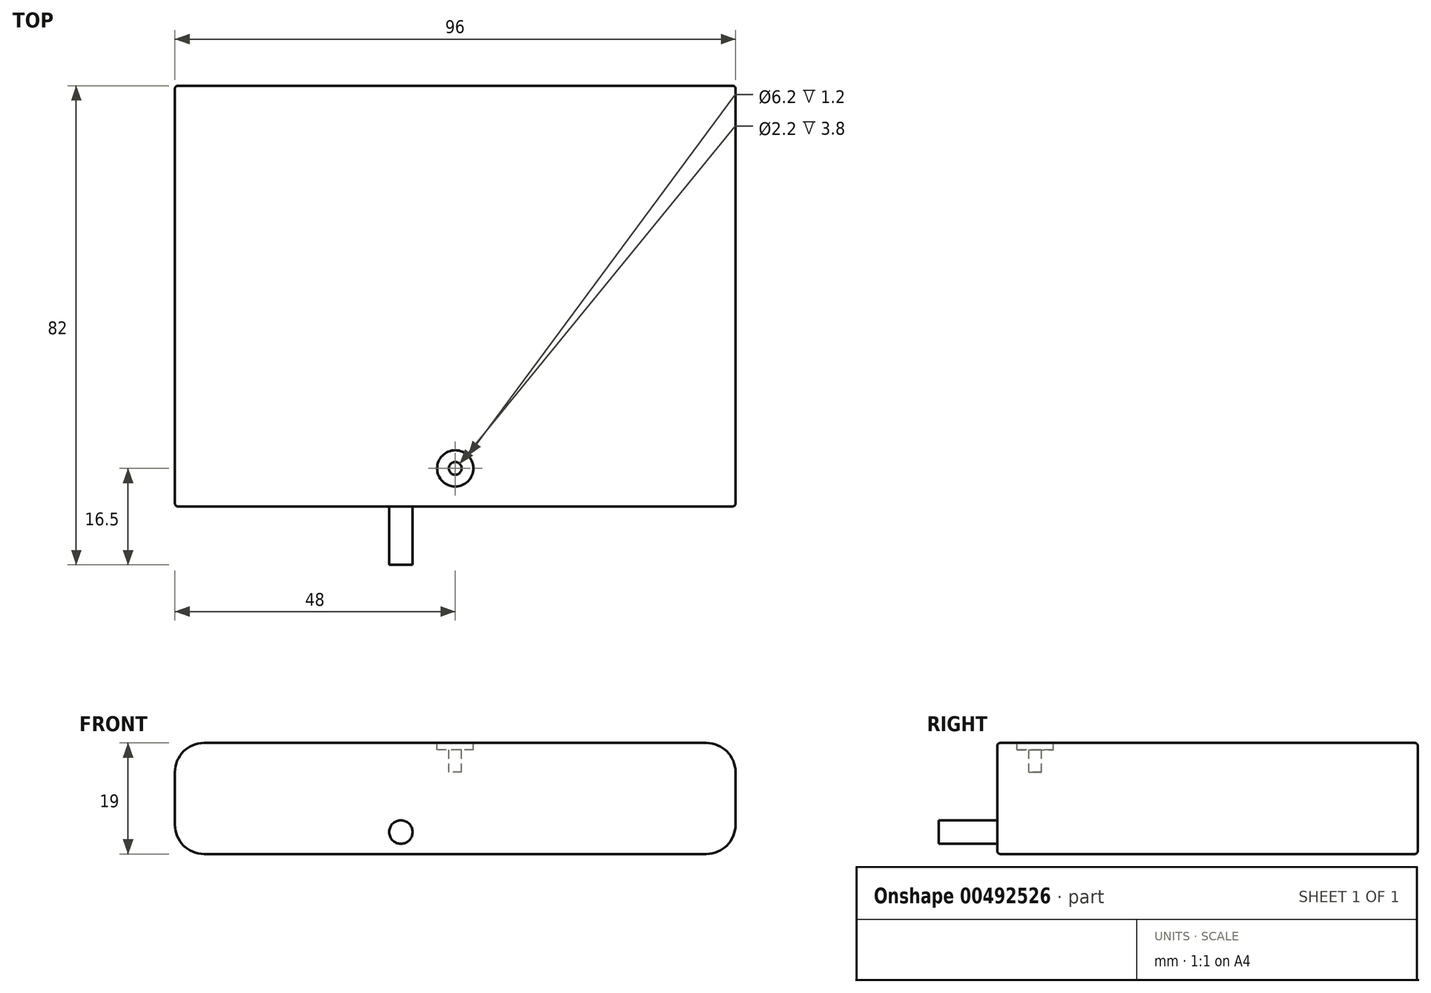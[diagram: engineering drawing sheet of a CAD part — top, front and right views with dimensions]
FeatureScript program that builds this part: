
annotation { "Feature Type Name" : "Feature", "Feature Type Description" : "" }
export const myFeature = defineFeature(function(context is Context, id is Id, definition is map)
    precondition{}
    {
        {
            var Q0;
            Q0=qCreatedBy(makeId("Top.planeOp"),FACE);
            var sketch = newSketch(context, id + "F0", { "sketchPlane" : qUnion([Q0])});
            skLineSegment(sketch, "E0.bottom", {"start": v(48, 36) * mm, "end": v(-48, 36) * mm});
            skLineSegment(sketch, "E0.top", {"start": v(48, -36) * mm, "end": v(-48, -36) * mm});
            skLineSegment(sketch, "E0.left", {"start": v(48, 36) * mm, "end": v(48, -36) * mm});
            skLineSegment(sketch, "E0.right", {"start": v(-48, 36) * mm, "end": v(-48, -36) * mm});
            skPoint(sketch, "E0.middle", {"position": v(0, 0) * mm});
            skSolve(sketch);
        }
        {
            var Q0;
            Q0=qSketchRegion(id+"F0",true);
            extrude(context, id + "F1", {"entities" : qUnion([Q0]), "depth" : 19 * mm});
        }
        {
            var Q0;
            Q0=makeQuery(id+"F1.opExtrude","CAP_EDGE",EDGE,{"disambiguationData":[OSD([sQuery(id+"F0.wireOp",EDGE,"E0.left")])],"isStart":false});
            var Q1;
            Q1=makeQuery(id+"F1.opExtrude","CAP_EDGE",EDGE,{"disambiguationData":[OSD([sQuery(id+"F0.wireOp",EDGE,"E0.left")])],"isStart":true});
            var Q2;
            Q2=makeQuery(id+"F1.opExtrude","CAP_EDGE",EDGE,{"disambiguationData":[OSD([sQuery(id+"F0.wireOp",EDGE,"E0.right")])],"isStart":false});
            var Q3;
            Q3=makeQuery(id+"F1.opExtrude","CAP_EDGE",EDGE,{"disambiguationData":[OSD([sQuery(id+"F0.wireOp",EDGE,"E0.right")])],"isStart":true});
            fillet(context, id + "F2", {"entities" : qUnion([Q0, Q1, Q2, Q3]), "radius" : 5 * mm, "tangentPropagation" : true, "allowEdgeOverflow" : false});
        }
        {
            var Q0;
            Q0=makeQuery(id+"F1.opExtrude","SWEPT_FACE",FACE,{"disambiguationData":[OSD([sQuery(id+"F0.wireOp",EDGE,"E0.top")])]});
            var Q1;
            Q1=makeQuery(id+"F1.opExtrude","SWEPT_FACE",FACE,{"disambiguationData":[OSD([sQuery(id+"F0.wireOp",EDGE,"E0.bottom")])]});
            fillet(context, id + "F3", {"entities" : qUnion([Q0, Q1]), "radius" : .5 * mm, "tangentPropagation" : true, "allowEdgeOverflow" : false});
        }
        {
            var Q0;
            Q0=makeQuery(id+"F1.opExtrude","SWEPT_FACE",FACE,{"disambiguationData":[OSD([sQuery(id+"F0.wireOp",EDGE,"E0.top")])]});
            var sketch = newSketch(context, id + "F4", { "sketchPlane" : qUnion([Q0])});
            skCircle(sketch, "E1", {"center": v(-9.3, 3.75) * mm, "radius": 2 * mm});
            skSolve(sketch);
        }
        {
            var Q0;
            Q0=qSketchRegion(id+"F4",true);
            extrude(context, id + "F5", {"entities" : qUnion([Q0]), "operationType" : NewBodyOperationType.ADD, "depth" : 10 * mm});
        }
        {
            var Q0;
            Q0=makeQuery(id+"F1.opExtrude","CAP_FACE",FACE,{"disambiguationData":[OSD([sQuery(id+"F0.wireOp",EDGE,"E0.bottom"),sQuery(id+"F0.wireOp",EDGE,"E0.top"),sQuery(id+"F0.wireOp",EDGE,"E0.left"),sQuery(id+"F0.wireOp",EDGE,"E0.right")])],"isStart":false});
            var sketch = newSketch(context, id + "F6", { "sketchPlane" : qUnion([Q0])});
            skCircle(sketch, "E2", {"center": v(0, -29.5) * mm, "radius": 3.1 * mm});
            skCircle(sketch, "E3", {"center": v(0, -29.5) * mm, "radius": 1.1 * mm});
            skSolve(sketch);
        }
        {
            var Q0;
            Q0=makeQuery(id+"F6.imprint","IMPRINT",FACE,{"disambiguationData":[TD([[makeQuery(id+"F6.imprint","IMPRINT",EDGE,{"derivedFrom":sQuery(id+"F6.wireOp",EDGE,"E3")}),1.0]])]});
            extrude(context, id + "F7", {"entities" : qUnion([Q0]), "operationType" : NewBodyOperationType.REMOVE, "oppositeDirection" : true, "depth" : 5 * mm});
        }
        {
            var Q0;
            Q0=makeQuery(id+"F6.imprint","IMPRINT",FACE,{"disambiguationData":[TD([[makeQuery(id+"F6.imprint","IMPRINT",EDGE,{"derivedFrom":sQuery(id+"F6.wireOp",EDGE,"E2")}),1.0]])]});
            extrude(context, id + "F8", {"entities" : qUnion([Q0]), "operationType" : NewBodyOperationType.REMOVE, "oppositeDirection" : true, "depth" : 1.2 * mm});
        }
    });
